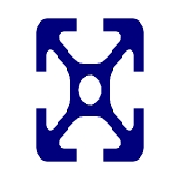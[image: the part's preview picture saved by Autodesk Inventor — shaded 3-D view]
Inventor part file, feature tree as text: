
AUTODESK INVENTOR PART (.ipt)
format: ipt  version: 2020 (Build 240168000, 168)  size: 274,432 bytes
history: native  units: mm
features: other x16, sketch x8
ambient origin geometry x8: Origin, YZ Plane, XZ Plane, XY Plane, X Axis, Y Axis, Z Axis, Center Point
bodies: Body (feature_tree)
feature tree (24):
  other  "Řízená délka"
  other  "Těleso1"
  other  "Start Plane"
  other  "End Plane"
  other  "iFeatureSketch"
  other  "DRAZKA_20:1"
  other  "DRAZKA_20:2"
  other  "DRAZKA_20:3"
  other  "DRAZKA_20:4"
  other  "DIRA_20:1"
  other  "DRAZKA_20:1Axis"
  other  "DRAZKA_20:2Axis"
  other  "DRAZKA_20:3Axis"
  other  "DRAZKA_20:4Axis"
  other  "DIRA_20:1Axis"
  sketch  "Sketch"  dims[d2=20.0mm d3=20.0mm d4=2.0mm d9=-0.0mm d10=110.0mm d11=0.13mm d12=0.0mm d15=0.83mm d16=0.83mm d17=9.8mm d18=3.0mm d19=4.55mm d20=45.0deg d21=5.2mm d22=1.8mm d24=1.0mm d26=0.83mm d27=0.83mm d28=9.8mm d29=3.0mm d30=4.55mm d31=45.0deg d32=5.2mm d33=1.8mm d35=1.0mm d37=0.83mm d38=0.83mm d39=9.8mm d40=3.0mm d41=4.55mm d42=45.0deg d43=5.2mm d44=1.8mm d46=1.0mm d48=0.83mm d49=0.83mm d50=9.8mm d51=3.0mm d52=4.55mm d53=45.0deg d54=5.2mm d55=1.8mm d57=1.0mm d59=4.3mm d60=0.0mm d61=0.0mm d62=0.0mm d63=0.0mm d64=0.0mm d65=0.0mm d66=0.0mm d67=0.0mm d76=90.0deg d14=110.0mm]
  sketch  "Náčrt11"
  other  "Pracovní rovina4"
  sketch  "Náčrt12"
  sketch  "Náčrt6"
  sketch  "Náčrt7"
  sketch  "Náčrt8"
  sketch  "Náčrt9"
  sketch  "Náčrt10"
